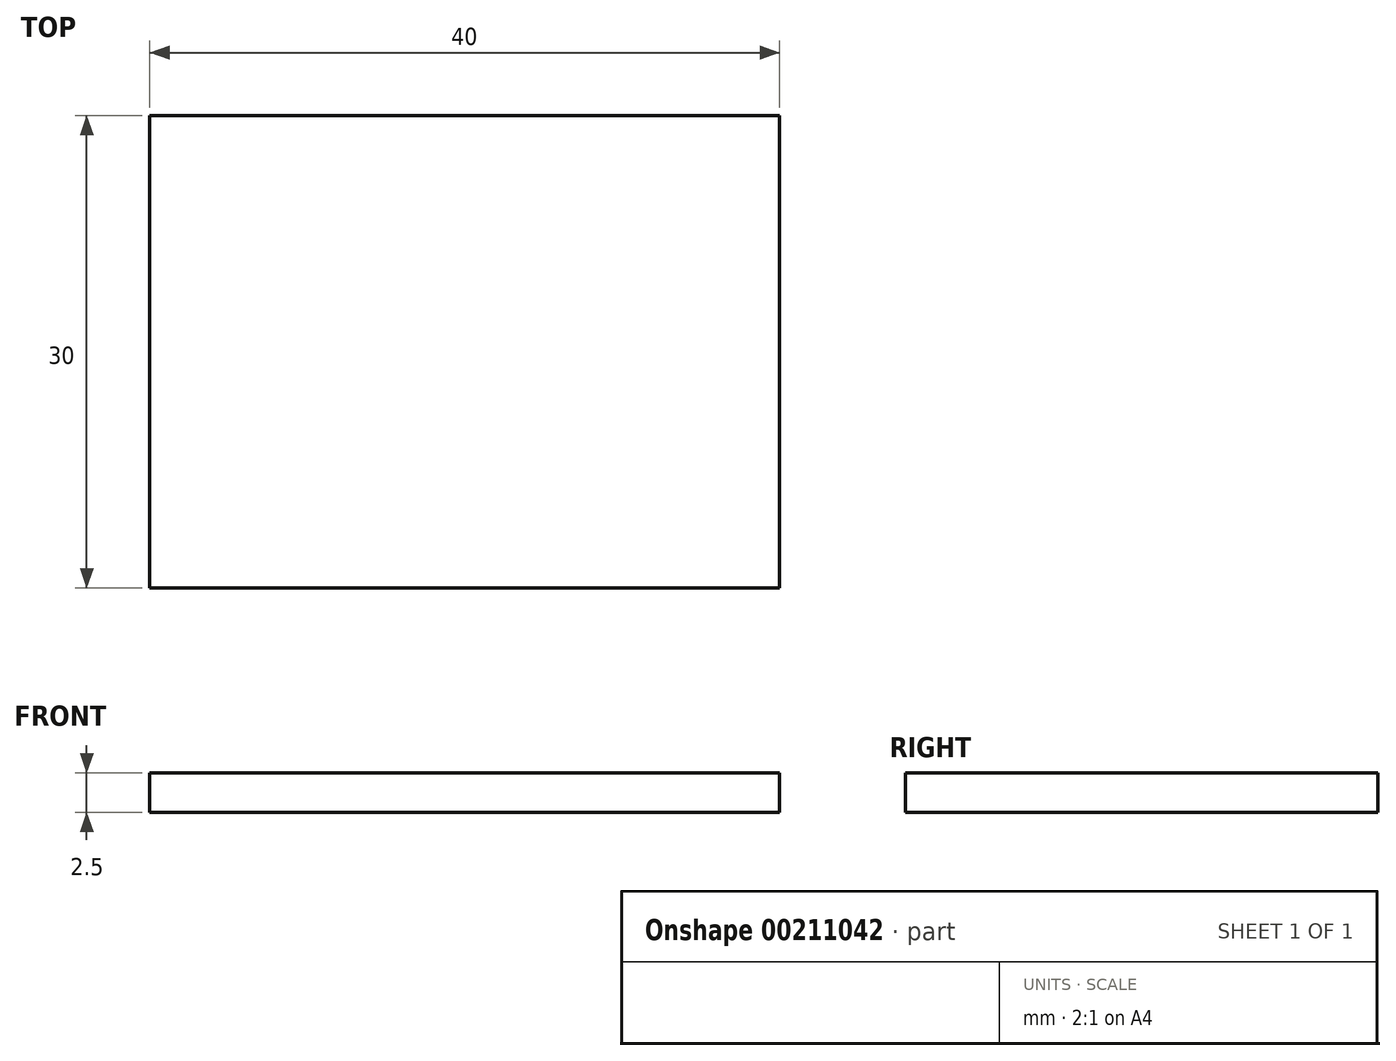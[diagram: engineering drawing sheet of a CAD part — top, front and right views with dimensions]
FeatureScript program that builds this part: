
annotation { "Feature Type Name" : "Feature", "Feature Type Description" : "" }
export const myFeature = defineFeature(function(context is Context, id is Id, definition is map)
    precondition{}
    {
        {
            var Q0;
            Q0=qCreatedBy(makeId("Top.planeOp"),FACE);
            var sketch = newSketch(context, id + "F0", { "sketchPlane" : qUnion([Q0])});
            skLineSegment(sketch, "E0.bottom", {"start": v(-13.68, 14.94) * mm, "end": v(26.32, 14.94) * mm});
            skLineSegment(sketch, "E0.top", {"start": v(-13.68, -15.06) * mm, "end": v(26.32, -15.06) * mm});
            skLineSegment(sketch, "E0.left", {"start": v(-13.68, 14.94) * mm, "end": v(-13.68, -15.06) * mm});
            skLineSegment(sketch, "E0.right", {"start": v(26.32, 14.94) * mm, "end": v(26.32, -15.06) * mm});
            skSolve(sketch);
        }
        {
            var Q0;
            Q0=makeQuery(id+"F0.imprint","IMPRINT",FACE,{"disambiguationData":[TD([[makeQuery(id+"F0.imprint","IMPRINT",EDGE,{"derivedFrom":sQuery(id+"F0.wireOp",EDGE,"E0.bottom")}),-1.0]])]});
            extrude(context, id + "F1", {"entities" : qUnion([Q0]), "depth" : 2.5 * mm});
        }
    });
